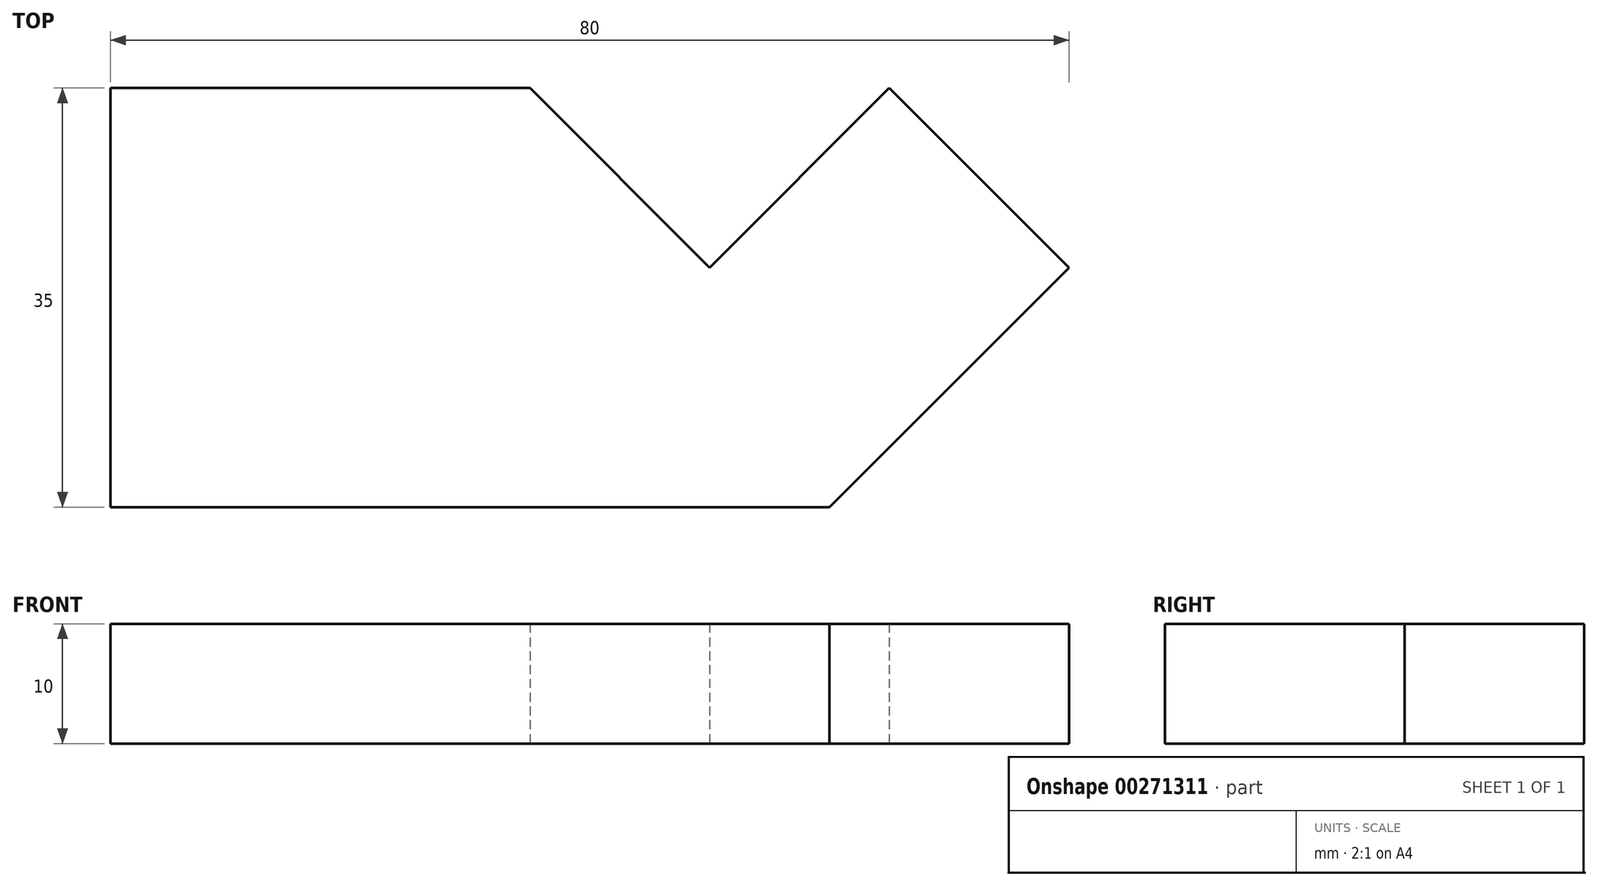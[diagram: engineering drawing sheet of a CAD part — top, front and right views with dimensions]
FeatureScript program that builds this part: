
annotation { "Feature Type Name" : "Feature", "Feature Type Description" : "" }
export const myFeature = defineFeature(function(context is Context, id is Id, definition is map)
    precondition{}
    {
        {
            var Q0;
            Q0=qCreatedBy(makeId("Top.planeOp"),FACE);
            var sketch = newSketch(context, id + "F0", { "sketchPlane" : qUnion([Q0])});
            skLineSegment(sketch, "E0.bottom", {"start": v(0, 0) * mm, "end": v(60, 0) * mm});
            skLineSegment(sketch, "E0.top", {"start": v(0, 35) * mm, "end": v(35, 35) * mm});
            skLineSegment(sketch, "E0.left", {"start": v(0, 0) * mm, "end": v(0, 35) * mm});
            skPoint(sketch, "E1", {"position": v(50, 20) * mm});
            skLineSegment(sketch, "E2", {"start": v(50, 20) * mm, "end": v(65, 35) * mm});
            skLineSegment(sketch, "E3", {"start": v(50, 20) * mm, "end": v(35, 35) * mm});
            skLineSegment(sketch, "E4", {"start": v(65, 35) * mm, "end": v(80, 20) * mm});
            skPoint(sketch, "E5", {"position": v(80, 20) * mm});
            skLineSegment(sketch, "E6", {"start": v(80, 20) * mm, "end": v(60, 0) * mm});
            skSolve(sketch);
        }
        {
            var Q0;
            Q0 = qSketchRegion(id + "F0", true);
            extrude(context, id + "F1", {"entities" : qUnion([Q0]), "depth" : 10 * mm});
        }
    });
